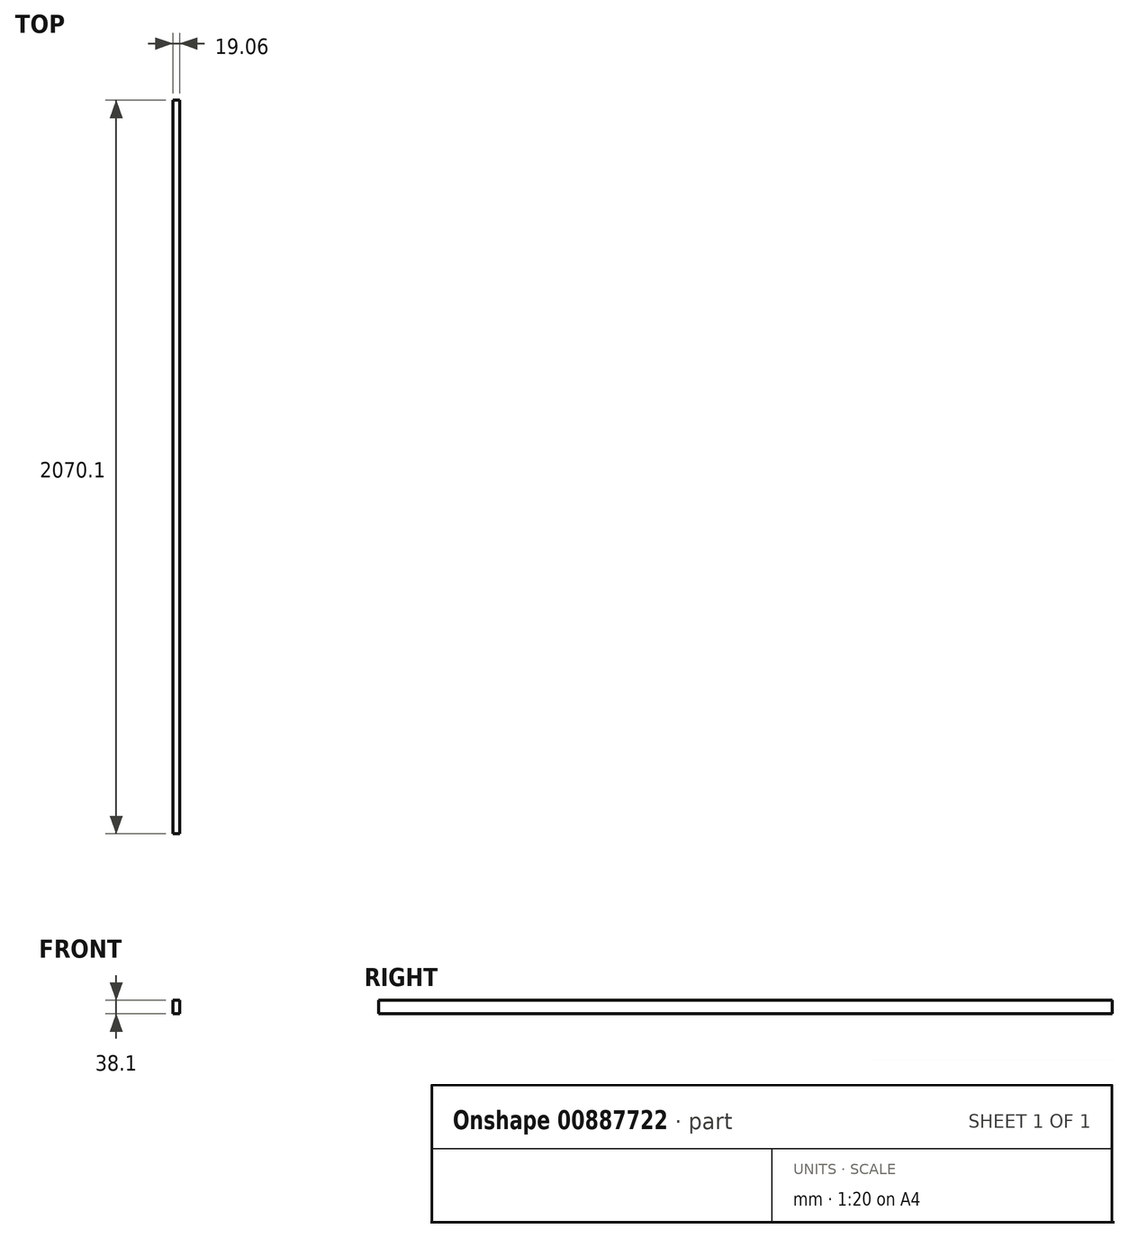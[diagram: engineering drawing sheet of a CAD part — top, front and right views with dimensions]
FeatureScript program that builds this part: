
annotation { "Feature Type Name" : "Feature", "Feature Type Description" : "" }
export const myFeature = defineFeature(function(context is Context, id is Id, definition is map)
    precondition{}
    {
        {
            var Q0;
            Q0=qCreatedBy(makeId("Front.planeOp"),FACE);
            var sketch = newSketch(context, id + "F0", { "sketchPlane" : qUnion([Q0])});
            skLineSegment(sketch, "E0.bottom", {"start": v(-9.52, 19.05) * mm, "end": v(9.53, 19.05) * mm});
            skLineSegment(sketch, "E0.top", {"start": v(-9.53, -19.05) * mm, "end": v(9.52, -19.05) * mm});
            skLineSegment(sketch, "E0.left", {"start": v(-9.52, 19.05) * mm, "end": v(-9.53, -19.05) * mm});
            skLineSegment(sketch, "E0.right", {"start": v(9.53, 19.05) * mm, "end": v(9.52, -19.05) * mm});
            skPoint(sketch, "E0.middle", {"position": v(0, 0) * mm});
            skSolve(sketch);
        }
        {
            var Q0;
            Q0 = qSketchRegion(id + "F0", true);
            extrude(context, id + "F1", {"entities" : qUnion([Q0]), "endBound" : BoundingType.SYMMETRIC, "depth" : 2070.1 * mm, "offsetDistance" : 25.4 * mm});
        }
    });
